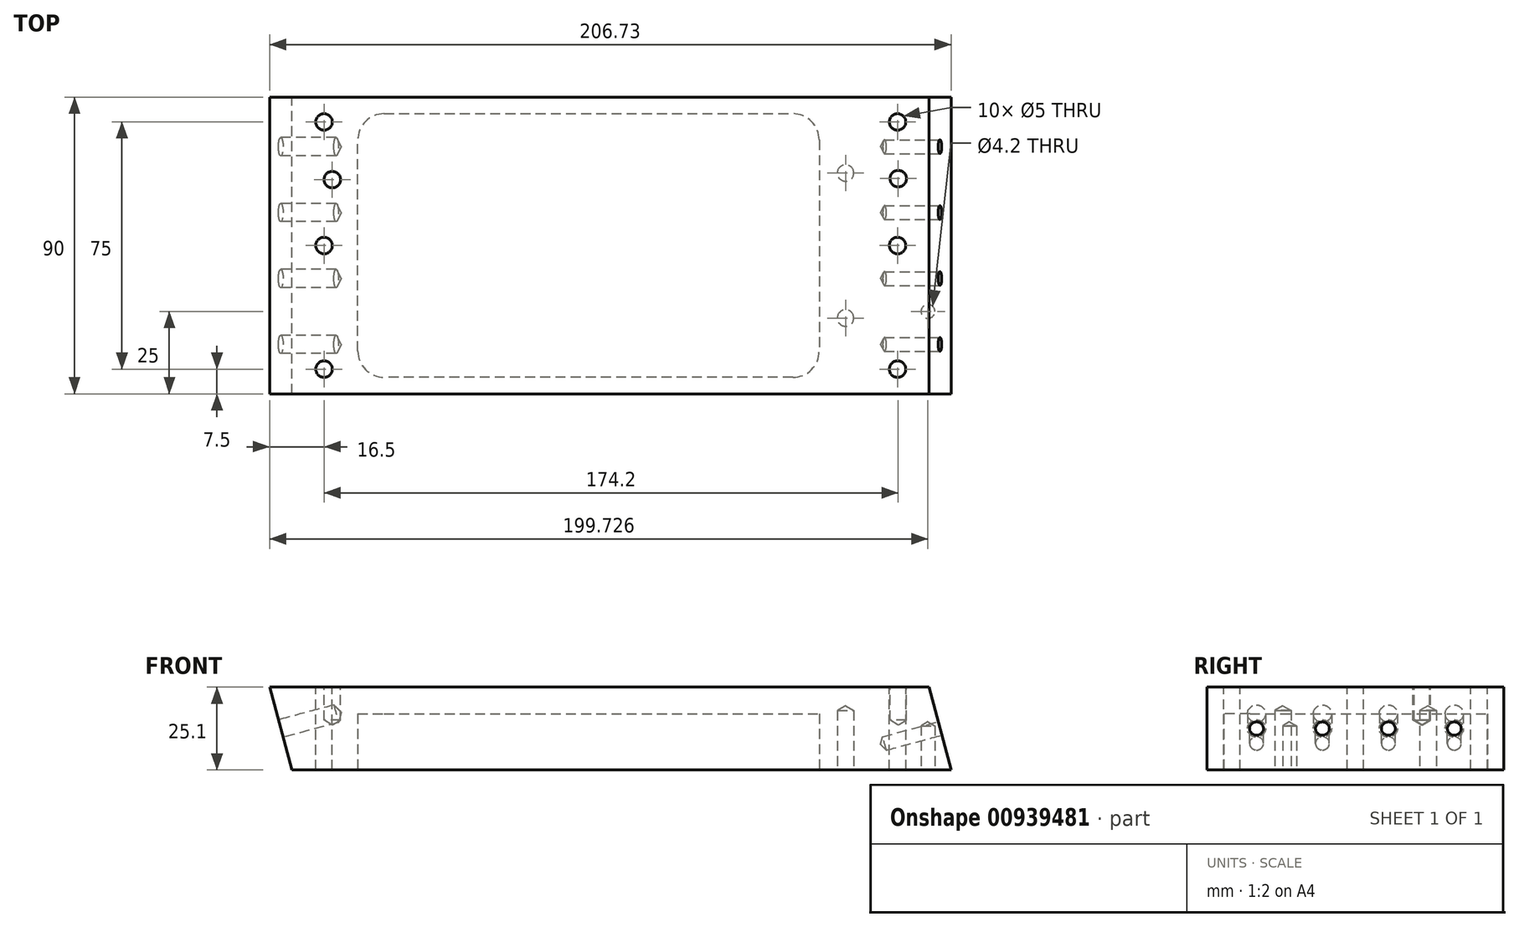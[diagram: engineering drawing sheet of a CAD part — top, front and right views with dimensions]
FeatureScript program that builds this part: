
annotation { "Feature Type Name" : "Feature", "Feature Type Description" : "" }
export const myFeature = defineFeature(function(context is Context, id is Id, definition is map)
    precondition{}
    {
        {
            var Q0;
            Q0=qCreatedBy(makeId("Front.planeOp"),FACE);
            var sketch = newSketch(context, id + "F0", { "sketchPlane" : qUnion([Q0])});
            skLineSegment(sketch, "E0", {"start": v(0, 0) * mm, "end": v(200, 0) * mm});
            skLineSegment(sketch, "E1", {"start": v(0, 0) * mm, "end": v(6.73, -25.1) * mm});
            skLineSegment(sketch, "E2", {"start": v(6.73, -25.1) * mm, "end": v(206.73, -25.1) * mm});
            skLineSegment(sketch, "E3", {"start": v(200, 0) * mm, "end": v(206.73, -25.1) * mm});
            skSolve(sketch);
        }
        {
            var Q0;
            Q0=makeQuery(id+"F0.imprint","IMPRINT",FACE,{"disambiguationData":[TD([[makeQuery(id+"F0.imprint","IMPRINT",EDGE,{"derivedFrom":sQuery(id+"F0.wireOp",EDGE,"E0")}),-1.0]])]});
            extrude(context, id + "F1", {"entities" : qUnion([Q0]), "depth" : 90 * mm, "offsetDistance" : 25 * mm});
        }
        {
            var Q0;
            Q0=makeQuery(id+"F1.opExtrude","SWEPT_FACE",FACE,{"disambiguationData":[OSD([sQuery(id+"F0.wireOp",EDGE,"E2")])]});
            var sketch = newSketch(context, id + "F2", { "sketchPlane" : qUnion([Q0])});
            skLineSegment(sketch, "E4", {"start": v(206.73, 45) * mm, "end": v(166.73, 45) * mm, "construction": true});
            skPoint(sketch, "E5", {"position": v(166.73, 45) * mm});
            skPoint(sketch, "E6", {"position": v(26.73, 45) * mm});
            skPoint(sketch, "E7", {"position": v(106.73, 85) * mm});
            skPoint(sketch, "E7.positionSnap0", {"position": v(106.73, 90) * mm});
            skPoint(sketch, "E8", {"position": v(106.73, 5) * mm});
            skPoint(sketch, "E8.positionSnap0", {"position": v(106.73, 0) * mm});
            skLineSegment(sketch, "E9", {"start": v(106.73, 85) * mm, "end": v(34.73, 85) * mm});
            skLineSegment(sketch, "E10", {"start": v(26.73, 77) * mm, "end": v(26.73, 13) * mm});
            skLineSegment(sketch, "E11", {"start": v(34.73, 5) * mm, "end": v(158.73, 5) * mm});
            skLineSegment(sketch, "E12", {"start": v(166.73, 13) * mm, "end": v(166.73, 77) * mm});
            skLineSegment(sketch, "E13", {"start": v(158.73, 85) * mm, "end": v(106.73, 85) * mm});
            skLineSegment(sketch, "E14.trimOffspring", {"start": v(26.73, 45) * mm, "end": v(6.73, 45) * mm, "construction": true});
            skPoint(sketch, "E15.visualSharp", {"position": v(26.73, 85) * mm});
            skArc(sketch, "E15.filletArc", {"start": v(34.73, 85) * mm, "mid": v(29.07, 82.66) * mm, "end": v(26.73, 77) * mm});
            skPoint(sketch, "E16.visualSharp", {"position": v(26.73, 5) * mm});
            skArc(sketch, "E16.filletArc", {"start": v(26.73, 13) * mm, "mid": v(29.07, 7.34) * mm, "end": v(34.73, 5) * mm});
            skPoint(sketch, "E17.visualSharp", {"position": v(166.73, 5) * mm});
            skArc(sketch, "E17.filletArc", {"start": v(158.73, 5) * mm, "mid": v(164.38, 7.34) * mm, "end": v(166.73, 13) * mm});
            skPoint(sketch, "E18.visualSharp", {"position": v(166.73, 85) * mm});
            skArc(sketch, "E18.filletArc", {"start": v(166.73, 77) * mm, "mid": v(164.38, 82.66) * mm, "end": v(158.73, 85) * mm});
            skSolve(sketch);
        }
        {
            var Q0;
            Q0=makeQuery(id+"F2.imprint","IMPRINT",FACE,{"disambiguationData":[TD([[makeQuery(id+"F2.imprint","IMPRINT",EDGE,{"derivedFrom":sQuery(id+"F2.wireOp",EDGE,"E9")}),1.0]])]});
            extrude(context, id + "F3", {"entities" : qUnion([Q0]), "operationType" : NewBodyOperationType.REMOVE, "oppositeDirection" : true, "depth" : 17 * mm, "offsetDistance" : 25 * mm});
        }
        {
            var Q0;
            Q0=makeQuery(id+"F1.opExtrude","SWEPT_FACE",FACE,{"disambiguationData":[OSD([sQuery(id+"F0.wireOp",EDGE,"E1")])]});
            var sketch = newSketch(context, id + "F4", { "sketchPlane" : qUnion([Q0])});
            skLineSegment(sketch, "E19.bottom", {"start": v(0, 0) * mm, "end": v(90, 0) * mm});
            skLineSegment(sketch, "E19.top", {"start": v(0, -25.99) * mm, "end": v(90, -25.99) * mm});
            skLineSegment(sketch, "E19.left", {"start": v(0, 0) * mm, "end": v(0, -25.99) * mm});
            skLineSegment(sketch, "E19.right", {"start": v(90, 0) * mm, "end": v(90, -25.99) * mm});
            skPoint(sketch, "E20", {"position": v(0, -13) * mm});
            skPoint(sketch, "E21", {"position": v(15, -13) * mm});
            skPoint(sketch, "E22", {"position": v(90, -13) * mm});
            skPoint(sketch, "E23", {"position": v(75, -13) * mm});
            skPoint(sketch, "E24", {"position": v(35, -13) * mm});
            skPoint(sketch, "E25", {"position": v(55, -13) * mm});
            skLineSegment(sketch, "E26", {"start": v(0, -13) * mm, "end": v(90, -13) * mm});
            skSolve(sketch);
        }
        {
            var Q0;
            Q0=sQuery(id+"F4.wireOp",VERTEX,"E21");
            var Q1;
            Q1=sQuery(id+"F4.wireOp",VERTEX,"E24");
            var Q2;
            Q2=sQuery(id+"F4.wireOp",VERTEX,"E25");
            var Q3;
            Q3=sQuery(id+"F4.wireOp",VERTEX,"E23");
            var Q4;
            Q4=makeQuery(id+"F1.opExtrude","SWEPT_BODY",BODY,{"disambiguationData":[OSD([sQuery(id+"F0.wireOp",EDGE,"E0"),sQuery(id+"F0.wireOp",EDGE,"E1"),sQuery(id+"F0.wireOp",EDGE,"E2"),sQuery(id+"F0.wireOp",EDGE,"E3")])]});
            hole(context, id + "F5", {"style" : HoleStyle.SIMPLE, "endStyle" : HoleEndStyle.BLIND, "standardTappedOrClearance" : lookupTablePath({ "fit" : "Normal", "standard" : "ISO", "size" : "M5", "type" : "Clearance" }), "standardBlindInLast" : lookupTablePath({ "fit" : "Normal", "standard" : "ISO", "engagement" : "75%", "pitch" : "0.8 mm", "size" : "M5", "type" : "Clearance & tapped" }), "holeDiameter" : 5.5 * mm, "majorDiameter" : 5 * mm, "holeDepth" : 17.4 * mm, "isTappedThrough" : true, "tappedDepth" : 15 * mm, "tapClearance" : 3, "locations" : qUnion([Q0, Q1, Q2, Q3]), "scope" : qUnion([Q4])});
        }
        {
            var Q0;
            Q0=makeQuery(id+"F1.opExtrude","SWEPT_FACE",FACE,{"disambiguationData":[OSD([sQuery(id+"F0.wireOp",EDGE,"E0")])]});
            var sketch = newSketch(context, id + "F6", { "sketchPlane" : qUnion([Q0])});
            skPoint(sketch, "E27", {"position": v(16.5, -45) * mm});
            skPoint(sketch, "E27.positionSnap0", {"position": v(0, -45) * mm});
            skPoint(sketch, "E28", {"position": v(190.5, -45) * mm});
            skPoint(sketch, "E28.positionSnap0", {"position": v(200, -45) * mm});
            skPoint(sketch, "E29", {"position": v(16.5, -7.5) * mm});
            skPoint(sketch, "E30", {"position": v(16.5, -82.5) * mm});
            skPoint(sketch, "E31", {"position": v(190.5, -7.5) * mm});
            skPoint(sketch, "E32", {"position": v(190.5, -82.5) * mm});
            skSolve(sketch);
        }
        {
            var Q0;
            Q0=sQuery(id+"F6.wireOp",VERTEX,"E29");
            var Q1;
            Q1=sQuery(id+"F6.wireOp",VERTEX,"E27");
            var Q2;
            Q2=sQuery(id+"F6.wireOp",VERTEX,"E30");
            var Q3;
            Q3=sQuery(id+"F6.wireOp",VERTEX,"E32");
            var Q4;
            Q4=sQuery(id+"F6.wireOp",VERTEX,"E28");
            var Q5;
            Q5=sQuery(id+"F6.wireOp",VERTEX,"E31");
            var Q6;
            Q6=makeQuery(id+"F1.opExtrude","SWEPT_BODY",BODY,{"disambiguationData":[OSD([sQuery(id+"F0.wireOp",EDGE,"E0"),sQuery(id+"F0.wireOp",EDGE,"E1"),sQuery(id+"F0.wireOp",EDGE,"E2"),sQuery(id+"F0.wireOp",EDGE,"E3")])]});
            hole(context, id + "F7", {"style" : HoleStyle.SIMPLE, "endStyle" : HoleEndStyle.THROUGH, "standardTappedOrClearance" : lookupTablePath({ "standard" : "ISO", "engagement" : "75%", "pitch" : "1 mm", "size" : "M6", "type" : "Tapped" }), "standardBlindInLast" : lookupTablePath({ "standard" : "ISO", "fit" : "Normal", "engagement" : "75%", "pitch" : "1 mm", "size" : "M6", "type" : "Clearance & tapped" }), "holeDiameter" : 5 * mm, "majorDiameter" : 6 * mm, "showTappedDepth" : true, "isTappedThrough" : true, "tappedDepth" : 15 * mm, "tapClearance" : 3, "locations" : qUnion([Q0, Q1, Q2, Q3, Q4, Q5]), "scope" : qUnion([Q6])});
        }
        {
            var Q0;
            Q0=makeQuery(id+"F1.opExtrude","SWEPT_FACE",FACE,{"disambiguationData":[OSD([sQuery(id+"F0.wireOp",EDGE,"E0")])]});
            var sketch = newSketch(context, id + "F8", { "sketchPlane" : qUnion([Q0])});
            skPoint(sketch, "E33", {"position": v(19, -25) * mm});
            skPoint(sketch, "E34", {"position": v(190.7, -24.7) * mm});
            skSolve(sketch);
        }
        {
            var Q0;
            Q0=sQuery(id+"F8.wireOp",VERTEX,"E33");
            var Q1;
            Q1=sQuery(id+"F8.wireOp",VERTEX,"E34");
            var Q2;
            Q2=makeQuery(id+"F1.opExtrude","SWEPT_BODY",BODY,{"disambiguationData":[OSD([sQuery(id+"F0.wireOp",EDGE,"E0"),sQuery(id+"F0.wireOp",EDGE,"E1"),sQuery(id+"F0.wireOp",EDGE,"E2"),sQuery(id+"F0.wireOp",EDGE,"E3")])]});
            hole(context, id + "F9", {"style" : HoleStyle.SIMPLE, "endStyle" : HoleEndStyle.BLIND, "holeDiameter" : 5 * mm, "majorDiameter" : 6 * mm, "holeDepth" : 10 * mm, "isTappedThrough" : true, "tappedDepth" : 15 * mm, "tapClearance" : 3, "locations" : qUnion([Q0, Q1]), "scope" : qUnion([Q2])});
        }
        {
            var Q0;
            Q0=makeQuery(id+"F1.opExtrude","SWEPT_FACE",FACE,{"disambiguationData":[OSD([sQuery(id+"F0.wireOp",EDGE,"E3")])]});
            var sketch = newSketch(context, id + "F10", { "sketchPlane" : qUnion([Q0])});
            skPoint(sketch, "E35", {"position": v(-15, -64.76) * mm});
            skPoint(sketch, "E35.positionSnap0", {"position": v(0, -64.76) * mm});
            skPoint(sketch, "E36", {"position": v(-75, -64.76) * mm});
            skPoint(sketch, "E36.positionSnap0", {"position": v(-90, -64.76) * mm});
            skPoint(sketch, "E37", {"position": v(-35, -64.76) * mm});
            skPoint(sketch, "E38", {"position": v(-55, -64.76) * mm});
            skSolve(sketch);
        }
        {
            var Q0;
            Q0=sQuery(id+"F10.wireOp",VERTEX,"E35");
            var Q1;
            Q1=sQuery(id+"F10.wireOp",VERTEX,"E37");
            var Q2;
            Q2=sQuery(id+"F10.wireOp",VERTEX,"E38");
            var Q3;
            Q3=sQuery(id+"F10.wireOp",VERTEX,"E36");
            var Q4;
            Q4=makeQuery(id+"F1.opExtrude","SWEPT_BODY",BODY,{"disambiguationData":[OSD([sQuery(id+"F0.wireOp",EDGE,"E0"),sQuery(id+"F0.wireOp",EDGE,"E1"),sQuery(id+"F0.wireOp",EDGE,"E2"),sQuery(id+"F0.wireOp",EDGE,"E3")])]});
            hole(context, id + "F11", {"style" : HoleStyle.SIMPLE, "endStyle" : HoleEndStyle.BLIND, "standardTappedOrClearance" : lookupTablePath({ "standard" : "ISO", "engagement" : "75%", "pitch" : "0.8 mm", "size" : "M5", "type" : "Tapped" }), "standardBlindInLast" : lookupTablePath({ "standard" : "ISO", "fit" : "Normal", "engagement" : "75%", "pitch" : "0.8 mm", "size" : "M5", "type" : "Clearance & tapped" }), "holeDiameter" : 4.2 * mm, "majorDiameter" : 5 * mm, "showTappedDepth" : true, "holeDepth" : 17.4 * mm, "isTappedThrough" : true, "tappedDepth" : 15 * mm, "tapClearance" : 3, "locations" : qUnion([Q0, Q1, Q2, Q3]), "scope" : qUnion([Q4])});
        }
        {
            var Q0;
            Q0=makeQuery(id+"F1.opExtrude","SWEPT_FACE",FACE,{"disambiguationData":[OSD([sQuery(id+"F0.wireOp",EDGE,"E2")])]});
            var sketch = newSketch(context, id + "F12", { "sketchPlane" : qUnion([Q0])});
            skPoint(sketch, "E39", {"position": v(199.73, 65) * mm});
            skSolve(sketch);
        }
        {
            var Q0;
            Q0=sQuery(id+"F12.wireOp",VERTEX,"E39");
            var Q1;
            Q1=makeQuery(id+"F1.opExtrude","SWEPT_BODY",BODY,{"disambiguationData":[OSD([sQuery(id+"F0.wireOp",EDGE,"E0"),sQuery(id+"F0.wireOp",EDGE,"E1"),sQuery(id+"F0.wireOp",EDGE,"E2"),sQuery(id+"F0.wireOp",EDGE,"E3")])]});
            hole(context, id + "F13", {"style" : HoleStyle.SIMPLE, "endStyle" : HoleEndStyle.BLIND, "standardTappedOrClearance" : lookupTablePath({ "standard" : "ISO", "engagement" : "75%", "pitch" : "0.8 mm", "size" : "M5", "type" : "Tapped" }), "standardBlindInLast" : lookupTablePath({ "standard" : "ISO", "fit" : "Normal", "engagement" : "75%", "pitch" : "0.8 mm", "size" : "M5", "type" : "Clearance & tapped" }), "holeDiameter" : 4.2 * mm, "majorDiameter" : 5 * mm, "showTappedDepth" : true, "holeDepth" : 13.4 * mm, "isTappedThrough" : true, "tappedDepth" : 11 * mm, "tapClearance" : 3, "locations" : qUnion([Q0]), "scope" : qUnion([Q1])});
        }
        {
            var Q0;
            Q0=makeQuery(id+"F1.opExtrude","SWEPT_FACE",FACE,{"disambiguationData":[OSD([sQuery(id+"F0.wireOp",EDGE,"E2")])]});
            var sketch = newSketch(context, id + "F14", { "sketchPlane" : qUnion([Q0])});
            skPoint(sketch, "E40", {"position": v(174.73, 67) * mm});
            skPoint(sketch, "E41", {"position": v(174.73, 23) * mm});
            skSolve(sketch);
        }
        {
            var Q0;
            Q0=sQuery(id+"F14.wireOp",VERTEX,"E40");
            var Q1;
            Q1=sQuery(id+"F14.wireOp",VERTEX,"E41");
            var Q2;
            Q2=makeQuery(id+"F1.opExtrude","SWEPT_BODY",BODY,{"disambiguationData":[OSD([sQuery(id+"F0.wireOp",EDGE,"E0"),sQuery(id+"F0.wireOp",EDGE,"E1"),sQuery(id+"F0.wireOp",EDGE,"E2"),sQuery(id+"F0.wireOp",EDGE,"E3")])]});
            hole(context, id + "F15", {"style" : HoleStyle.SIMPLE, "endStyle" : HoleEndStyle.BLIND, "standardTappedOrClearance" : lookupTablePath({ "standard" : "ISO", "engagement" : "75%", "pitch" : "1 mm", "size" : "M6", "type" : "Tapped" }), "standardBlindInLast" : lookupTablePath({ "standard" : "ISO", "fit" : "Normal", "engagement" : "75%", "pitch" : "1 mm", "size" : "M6", "type" : "Clearance & tapped" }), "holeDiameter" : 5 * mm, "majorDiameter" : 6 * mm, "showTappedDepth" : true, "holeDepth" : 18 * mm, "isTappedThrough" : true, "tappedDepth" : 15 * mm, "tapClearance" : 3, "locations" : qUnion([Q0, Q1]), "scope" : qUnion([Q2])});
        }
    });
